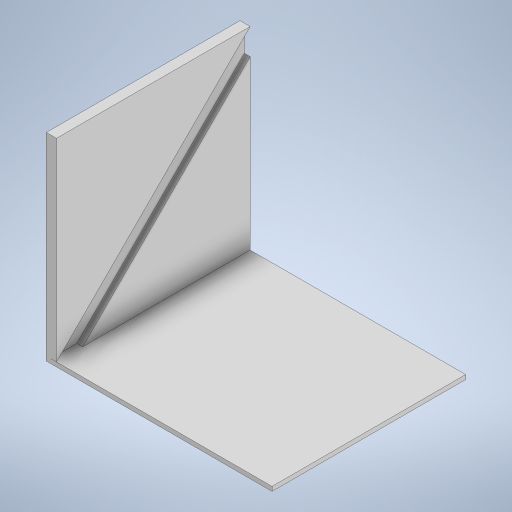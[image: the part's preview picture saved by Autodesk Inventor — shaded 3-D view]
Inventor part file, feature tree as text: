
AUTODESK INVENTOR PART (.ipt)
format: ipt  version: 2024 (Build 280153000, 153)  size: 323,072 bytes
history: native  units: mm
features: extrude x11, sketch x11
ambient origin geometry x8: Origin, YZ Plane, XZ Plane, XY Plane, X Axis, Y Axis, Z Axis, Center Point
bodies: Solid1 (feature_tree)
feature tree (22):
  extrude  "Top"  Depth=160.0mm
  extrude  "Right"  Depth=179.5mm
  extrude  "Left"  Depth=215.9mm
  extrude  "Plexiglass Cut"  Depth=25.4mm
  extrude  "Bottom"  Depth=266.7mm TaperAngle=0.0deg
  extrude  "Top Flattening"  Depth=266.7mm TaperAngle=0.0deg
  extrude  "Outer Side Flattening"  Depth=12.7mm TaperAngle=0.0deg
  extrude  "Bottom Flattening"  Depth=22.4mm TaperAngle=0.0deg
  extrude  "Inner Flattening"  Depth=22.389425mm
  extrude  "Top Cut"  Depth=22.4mm TaperAngle=0.0deg
  extrude  "Quarter Cut"  Depth=22.4mm TaperAngle=0.0deg
  sketch  "Sketch1"  dims[d11=220.0mm d12=160.0mm]
  sketch  "Sketch3"  dims[d15=248.6mm d16=179.5mm]
  sketch  "Sketch4"  dims[d18=304.8mm d19=215.9mm]
  sketch  "Sketch5"  dims[d20=25.4mm d21=0.0mm d22=25.4mm]
  sketch  "Sketch6"  dims[d25=266.7mm d26=50.8mm d27=0.0mm]
  sketch  "Sketch9"  dims[d28=266.7mm d29=50.8mm d30=0.0mm]
  sketch  "Sketch10"  dims[d31=12.7mm d32=304.8mm d33=0.0mm]
  sketch  "Sketch11"  dims[d34=25.4mm d35=0.0mm d46=22.4mm d47=0.0mm]
  sketch  "Sketch12"  dims[d48=22.389425mm d49=22.389425mm]
  sketch  "Sketch13"  dims[d50=0.0mm d51=0.0mm d52=22.4mm d53=0.0mm]
  sketch  "Sketch14"  dims[d54=296.8mm d55=22.4mm d56=0.0mm d57=0.0mm d58=0.0mm d59=0.0mm d60=0.0mm]
